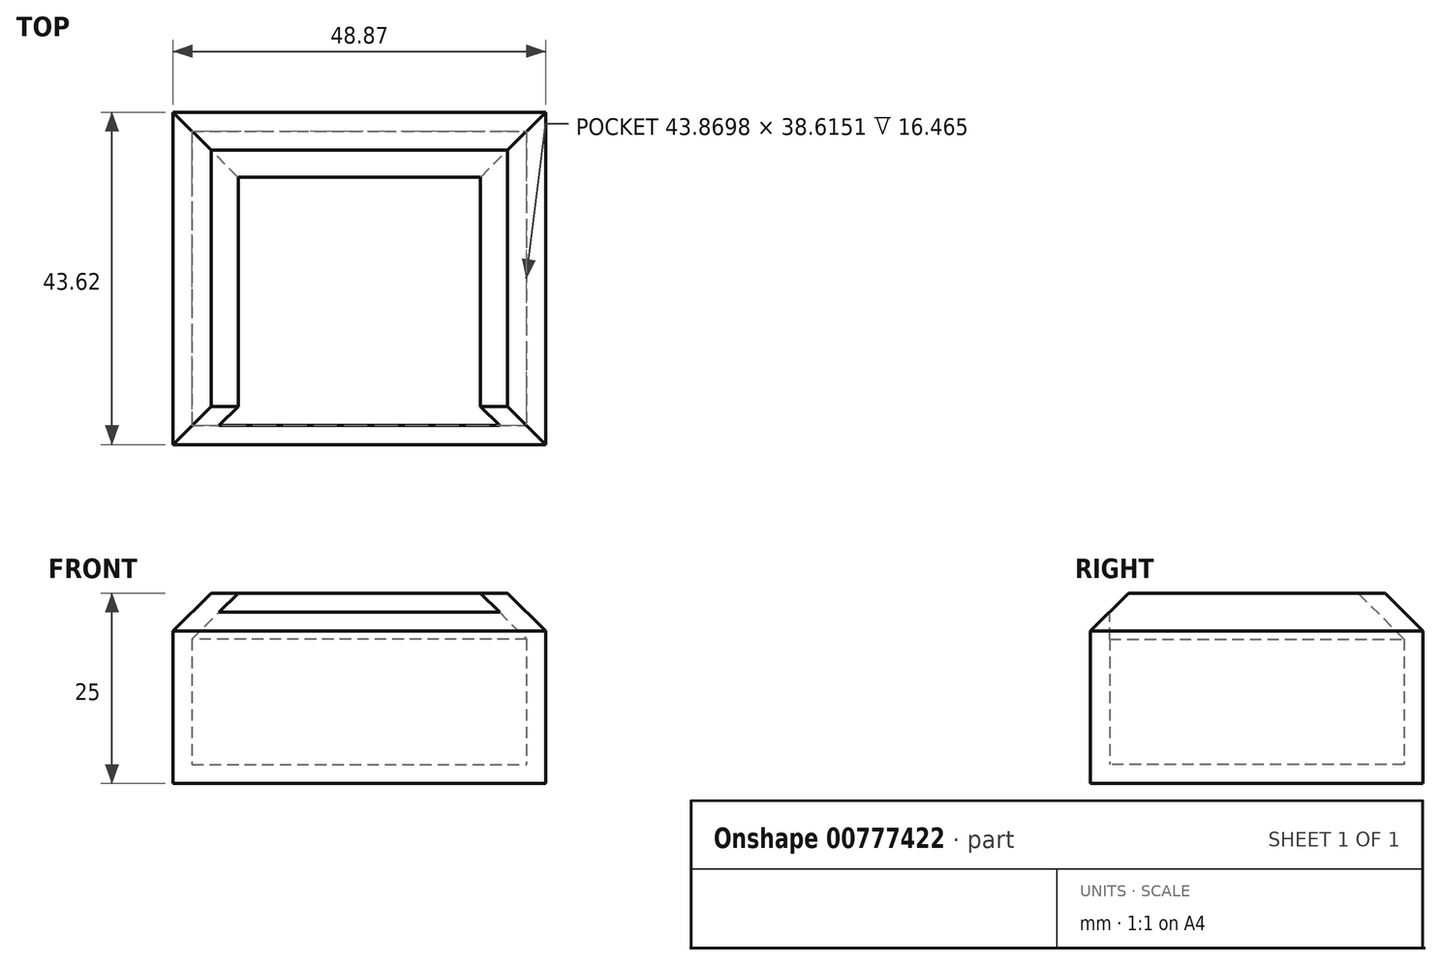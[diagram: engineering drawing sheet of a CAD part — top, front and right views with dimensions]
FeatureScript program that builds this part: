
annotation { "Feature Type Name" : "Feature", "Feature Type Description" : "" }
export const myFeature = defineFeature(function(context is Context, id is Id, definition is map)
    precondition{}
    {
        {
            var Q0;
            Q0=qCreatedBy(makeId("Top.planeOp"),FACE);
            var sketch = newSketch(context, id + "F0", { "sketchPlane" : qUnion([Q0])});
            skLineSegment(sketch, "E0.bottom", {"start": v(-135.6, 24.87) * mm, "end": v(-86.73, 24.87) * mm});
            skLineSegment(sketch, "E0.top", {"start": v(-135.6, -18.75) * mm, "end": v(-86.73, -18.75) * mm});
            skLineSegment(sketch, "E0.left", {"start": v(-135.6, 24.87) * mm, "end": v(-135.6, -18.75) * mm});
            skLineSegment(sketch, "E0.right", {"start": v(-86.73, 24.87) * mm, "end": v(-86.73, -18.75) * mm});
            skSolve(sketch);
        }
        {
            var Q0;
            Q0=makeQuery(id+"F0.imprint","IMPRINT",FACE,{"disambiguationData":[TD([[makeQuery(id+"F0.imprint","IMPRINT",EDGE,{"derivedFrom":sQuery(id+"F0.wireOp",EDGE,"E0.bottom")}),-1.0]])]});
            extrude(context, id + "F1", {"entities" : qUnion([Q0]), "depth" : 25 * mm, "offsetDistance" : 25 * mm});
        }
        {
            var Q0;
            Q0=makeQuery(id+"F1.opExtrude","CAP_FACE",FACE,{"disambiguationData":[OSD([sQuery(id+"F0.wireOp",EDGE,"E0.bottom"),sQuery(id+"F0.wireOp",EDGE,"E0.top"),sQuery(id+"F0.wireOp",EDGE,"E0.left"),sQuery(id+"F0.wireOp",EDGE,"E0.right")])],"isStart":false});
            chamfer(context, id + "F2", {"entities" : qUnion([Q0]), "width" : 5 * mm, "tangentPropagation" : true});
        }
        {
            var Q0;
            Q0=makeQuery(id+"F2.opChamfer","BLEND_FACE",FACE,{"disambiguationData":[OSD([sQuery(id+"F0.wireOp",EDGE,"E0.top")])]});
            var Q1;
            Q1=makeQuery(id+"F1.opExtrude","CAP_FACE",FACE,{"disambiguationData":[OSD([sQuery(id+"F0.wireOp",EDGE,"E0.bottom"),sQuery(id+"F0.wireOp",EDGE,"E0.top"),sQuery(id+"F0.wireOp",EDGE,"E0.left"),sQuery(id+"F0.wireOp",EDGE,"E0.right")])],"isStart":false});
            shell(context, id + "F3", {"entities" : qUnion([Q0, Q1]), "thickness" : 2.5 * mm});
        }
    });
